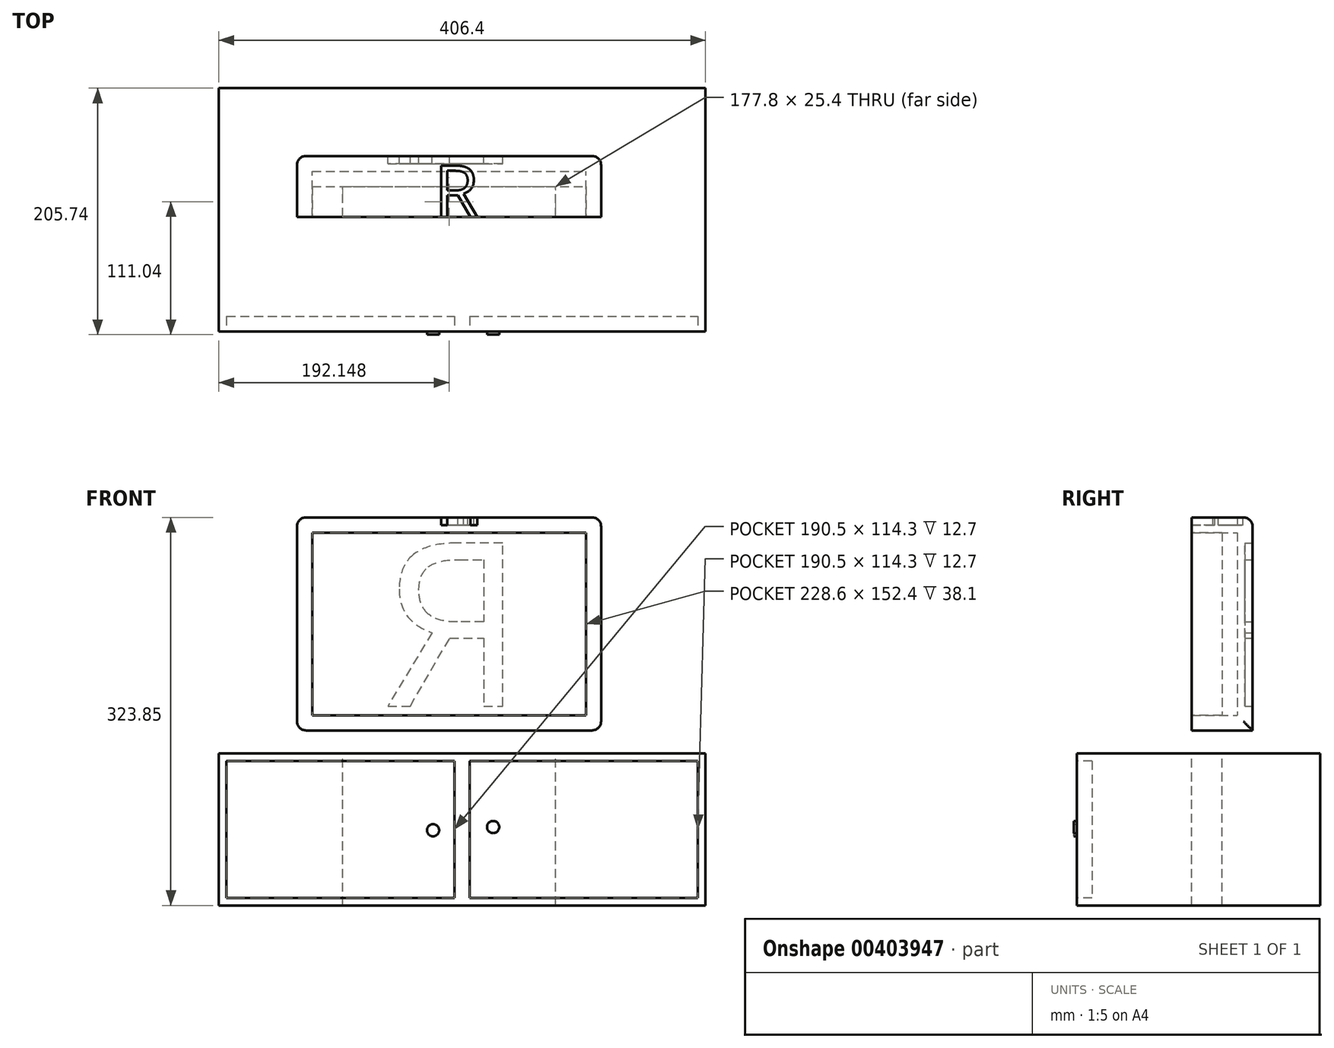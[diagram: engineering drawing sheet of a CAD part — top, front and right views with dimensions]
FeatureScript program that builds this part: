
annotation { "Feature Type Name" : "Feature", "Feature Type Description" : "" }
export const myFeature = defineFeature(function(context is Context, id is Id, definition is map)
    precondition{}
    {
        {
            var Q0;
            Q0=qCreatedBy(makeId("Front.planeOp"),FACE);
            var sketch = newSketch(context, id + "F0", { "sketchPlane" : qUnion([Q0])});
            skLineSegment(sketch, "E0.bottom", {"start": v(-146.56, 129.12) * mm, "end": v(107.44, 129.12) * mm});
            skLineSegment(sketch, "E0.top", {"start": v(-146.56, -48.68) * mm, "end": v(107.44, -48.68) * mm});
            skLineSegment(sketch, "E0.left", {"start": v(-146.56, 129.12) * mm, "end": v(-146.56, -48.68) * mm});
            skLineSegment(sketch, "E0.right", {"start": v(107.44, 129.12) * mm, "end": v(107.44, -48.68) * mm});
            skSolve(sketch);
        }
        {
            var Q0;
            Q0=makeQuery(id+"F0.imprint","IMPRINT",FACE,{"disambiguationData":[TD([[makeQuery(id+"F0.imprint","IMPRINT",EDGE,{"derivedFrom":sQuery(id+"F0.wireOp",EDGE,"E0.bottom")}),-1.0]])]});
            extrude(context, id + "F1", {"entities" : qUnion([Q0]), "depth" : 50.8 * mm});
        }
        {
            var Q0;
            Q0=makeQuery(id+"F1.opExtrude","CAP_FACE",FACE,{"disambiguationData":[OSD([sQuery(id+"F0.wireOp",EDGE,"E0.bottom"),sQuery(id+"F0.wireOp",EDGE,"E0.top"),sQuery(id+"F0.wireOp",EDGE,"E0.left"),sQuery(id+"F0.wireOp",EDGE,"E0.right")])],"isStart":false});
            shell(context, id + "F2", {"entities" : qUnion([Q0]), "thickness" : 12.7 * mm});
        }
        {
            var Q0;
            Q0=makeQuery(id+"F1.opExtrude","CAP_FACE",FACE,{"disambiguationData":[OSD([sQuery(id+"F0.wireOp",EDGE,"E0.bottom"),sQuery(id+"F0.wireOp",EDGE,"E0.top"),sQuery(id+"F0.wireOp",EDGE,"E0.left"),sQuery(id+"F0.wireOp",EDGE,"E0.right")])],"isStart":false});
            var sketch = newSketch(context, id + "F3", { "sketchPlane" : qUnion([Q0])});
            skLineSegment(sketch, "E1.bottom", {"start": v(-108.46, -48.68) * mm, "end": v(69.34, -48.68) * mm});
            skLineSegment(sketch, "E1.top", {"start": v(-108.46, -67.73) * mm, "end": v(69.34, -67.73) * mm});
            skLineSegment(sketch, "E1.left", {"start": v(-108.46, -48.68) * mm, "end": v(-108.46, -67.73) * mm});
            skLineSegment(sketch, "E1.right", {"start": v(69.34, -48.68) * mm, "end": v(69.34, -67.73) * mm});
            skSolve(sketch);
        }
        {
            var Q0;
            Q0 = qConstructionFilter(qBodyType(qCreatedBy(id + "F3" ,EDGE), BodyType.WIRE), ConstructionObject.NO);
            extrude(context, id + "F4", {"bodyType" : ToolBodyType.SURFACE, "surfaceEntities" : qUnion([Q0]), "oppositeDirection" : true, "depth" : 25.4 * mm});
        }
        {
            var Q0;
            Q0=makeQuery(id+"F4.opExtrude","SWEPT_FACE",FACE,{"disambiguationData":[OSD([sQuery(id+"F3.wireOp",EDGE,"E1.top")])]});
            var sketch = newSketch(context, id + "F5", { "sketchPlane" : qUnion([Q0])});
            skLineSegment(sketch, "E2.bottom", {"start": v(-211.7, -146.6) * mm, "end": v(194.7, -146.6) * mm});
            skLineSegment(sketch, "E2.top", {"start": v(-211.7, 56.6) * mm, "end": v(194.7, 56.6) * mm});
            skLineSegment(sketch, "E2.left", {"start": v(-211.7, -146.6) * mm, "end": v(-211.7, 56.6) * mm});
            skLineSegment(sketch, "E2.right", {"start": v(194.7, -146.6) * mm, "end": v(194.7, 56.6) * mm});
            skSolve(sketch);
        }
        {
            var Q0;
            Q0=makeQuery(id+"F5.imprint","IMPRINT",FACE,{"disambiguationData":[TD([[makeQuery(id+"F5.imprint","IMPRINT",EDGE,{"derivedFrom":sQuery(id+"F5.wireOp",EDGE,"E2.bottom")}),1.0]])]});
            extrude(context, id + "F6", {"entities" : qUnion([Q0]), "oppositeDirection" : true, "depth" : 127 * mm});
        }
        {
            var Q0;
            Q0=makeQuery(id+"F6.opExtrude","SWEPT_FACE",FACE,{"disambiguationData":[OSD([sQuery(id+"F5.wireOp",EDGE,"E2.bottom")])]});
            var sketch = newSketch(context, id + "F7", { "sketchPlane" : qUnion([Q0])});
            skLineSegment(sketch, "E3", {"start": v(-8.5, -67.73) * mm, "end": v(-8.5, -194.73) * mm});
            skPoint(sketch, "E3.endSnap0", {"position": v(-8.5, -194.73) * mm});
            skSolve(sketch);
        }
        {
            var Q0;
            {var subQ0=sQuery(id+"F7.wireOp",EDGE,"E3");Q0=makeQuery(id+"F7.imprint","IMPRINT",FACE,{"disambiguationData":[TD([[makeQuery(id+"F7.imprint","IMPRINT",EDGE,{"derivedFrom":subQ0}),-1.0]])]});}
            var sketch = newSketch(context, id + "F8", { "sketchPlane" : qUnion([Q0])});
            skLineSegment(sketch, "E4.bottom", {"start": v(-205.36, -74.08) * mm, "end": v(-14.86, -74.08) * mm});
            skLineSegment(sketch, "E4.top", {"start": v(-205.36, -188.38) * mm, "end": v(-14.86, -188.38) * mm});
            skLineSegment(sketch, "E4.left", {"start": v(-205.36, -74.08) * mm, "end": v(-205.36, -188.38) * mm});
            skLineSegment(sketch, "E4.right", {"start": v(-14.86, -74.08) * mm, "end": v(-14.86, -188.38) * mm});
            skLineSegment(sketch, "E5.bottom", {"start": v(-2.16, -74.08) * mm, "end": v(188.34, -74.08) * mm});
            skLineSegment(sketch, "E5.top", {"start": v(-2.16, -188.38) * mm, "end": v(188.34, -188.38) * mm});
            skLineSegment(sketch, "E5.left", {"start": v(-2.16, -74.08) * mm, "end": v(-2.16, -188.38) * mm});
            skLineSegment(sketch, "E5.right", {"start": v(188.34, -74.08) * mm, "end": v(188.34, -188.38) * mm});
            skSolve(sketch);
        }
        {
            var Q0;
            Q0 = qSketchRegion(id + "F8", true);
            extrude(context, id + "F9", {"entities" : qUnion([Q0]), "operationType" : NewBodyOperationType.REMOVE, "oppositeDirection" : true, "depth" : 12.7 * mm});
        }
        {
            var Q0;
            {var subQ0=sQuery(id+"F7.wireOp",EDGE,"E3");Q0=makeQuery(id+"F7.imprint","IMPRINT",FACE,{"disambiguationData":[TD([[makeQuery(id+"F7.imprint","IMPRINT",EDGE,{"derivedFrom":subQ0}),-1.0]])]});}
            var sketch = newSketch(context, id + "F10", { "sketchPlane" : qUnion([Q0])});
            skCircle(sketch, "E6", {"center": v(-32.88, -132.04) * mm, "radius": 5.08 * mm});
            skCircle(sketch, "E7", {"center": v(17.3, -129.32) * mm, "radius": 5.08 * mm});
            skSolve(sketch);
        }
        {
            var Q0;
            Q0=makeQuery(id+"F1.opExtrude","CAP_FACE",FACE,{"disambiguationData":[OSD([sQuery(id+"F0.wireOp",EDGE,"E0.bottom"),sQuery(id+"F0.wireOp",EDGE,"E0.top"),sQuery(id+"F0.wireOp",EDGE,"E0.left"),sQuery(id+"F0.wireOp",EDGE,"E0.right")])],"isStart":true});
            var sketch = newSketch(context, id + "F11", { "sketchPlane" : qUnion([Q0])});
            skText(sketch, "E8", { "text": "R", "fontName": "OpenSans-Regular.ttf"});
            const initialGuessF11  = {"E8": [-0.04394, -0.02836, 1, 0, 0.13731]};
            skSetInitialGuess(sketch, initialGuessF11);
            skSolve(sketch);
        }
        {
            var Q0;
            Q0 = qSketchRegion(id + "F11", true);
            extrude(context, id + "F12", {"entities" : qUnion([Q0]), "operationType" : NewBodyOperationType.REMOVE, "oppositeDirection" : true, "depth" : 6.35 * mm});
        }
        {
            var Q0;
            Q0=makeQuery(id+"F10.imprint","IMPRINT",FACE,{"disambiguationData":[TD([[makeQuery(id+"F10.imprint","IMPRINT",EDGE,{"derivedFrom":sQuery(id+"F10.wireOp",EDGE,"E6")}),1.0]])]});
            var Q1;
            Q1=makeQuery(id+"F10.imprint","IMPRINT",FACE,{"disambiguationData":[TD([[makeQuery(id+"F10.imprint","IMPRINT",EDGE,{"derivedFrom":sQuery(id+"F10.wireOp",EDGE,"E7")}),1.0]])]});
            extrude(context, id + "F13", {"entities" : qUnion([Q0, Q1]), "depth" : 2.54 * mm});
        }
        {
            var Q0;
            Q0=makeQuery(id+"F1.opExtrude","SWEPT_EDGE",EDGE,{"disambiguationData":[OSD([sQuery(id+"F0.wireOp",EDGE,"E0.bottom"),sQuery(id+"F0.wireOp",EDGE,"E0.right")])]});
            var Q1;
            Q1=makeQuery(id+"F1.opExtrude","CAP_EDGE",EDGE,{"disambiguationData":[OSD([sQuery(id+"F0.wireOp",EDGE,"E0.right")])],"isStart":true});
            var Q2;
            Q2=makeQuery(id+"F1.opExtrude","CAP_EDGE",EDGE,{"disambiguationData":[OSD([sQuery(id+"F0.wireOp",EDGE,"E0.bottom")])],"isStart":true});
            var Q3;
            Q3=makeQuery(id+"F1.opExtrude","SWEPT_EDGE",EDGE,{"disambiguationData":[OSD([sQuery(id+"F0.wireOp",EDGE,"E0.bottom"),sQuery(id+"F0.wireOp",EDGE,"E0.left")])]});
            var Q4;
            Q4=makeQuery(id+"F1.opExtrude","CAP_EDGE",EDGE,{"disambiguationData":[OSD([sQuery(id+"F0.wireOp",EDGE,"E0.left")])],"isStart":true});
            var Q5;
            Q5=makeQuery(id+"F1.opExtrude","SWEPT_EDGE",EDGE,{"disambiguationData":[OSD([sQuery(id+"F0.wireOp",EDGE,"E0.top"),sQuery(id+"F0.wireOp",EDGE,"E0.right")])]});
            var Q6;
            Q6=makeQuery(id+"F1.opExtrude","SWEPT_EDGE",EDGE,{"disambiguationData":[OSD([sQuery(id+"F0.wireOp",EDGE,"E0.top"),sQuery(id+"F0.wireOp",EDGE,"E0.left")])]});
            fillet(context, id + "F14", {"entities" : qUnion([Q0, Q1, Q2, Q3, Q4, Q5, Q6]), "radius" : 7.62 * mm, "tangentPropagation" : true, "allowEdgeOverflow" : false});
        }
        {
            var Q0;
            Q0=makeQuery(id+"F1.opExtrude","CAP_FACE",FACE,{"disambiguationData":[OSD([sQuery(id+"F0.wireOp",EDGE,"E0.bottom"),sQuery(id+"F0.wireOp",EDGE,"E0.top"),sQuery(id+"F0.wireOp",EDGE,"E0.left"),sQuery(id+"F0.wireOp",EDGE,"E0.right")])],"isStart":false});
            var sketch = newSketch(context, id + "F15", { "sketchPlane" : qUnion([Q0])});
            skLineSegment(sketch, "E9.bottom", {"start": v(-133.86, 116.42) * mm, "end": v(94.74, 116.42) * mm});
            skLineSegment(sketch, "E9.top", {"start": v(-133.86, -35.98) * mm, "end": v(94.74, -35.98) * mm});
            skLineSegment(sketch, "E9.left", {"start": v(-133.86, 116.42) * mm, "end": v(-133.86, -35.98) * mm});
            skLineSegment(sketch, "E9.right", {"start": v(94.74, 116.42) * mm, "end": v(94.74, -35.98) * mm});
            skSolve(sketch);
        }
        {
            var Q0;
            Q0=makeQuery(id+"F15.imprint","IMPRINT",FACE,{"disambiguationData":[TD([[makeQuery(id+"F15.imprint","IMPRINT",EDGE,{"derivedFrom":sQuery(id+"F15.wireOp",EDGE,"E9.bottom")}),-1.0]])]});
            extrude(context, id + "F16", {"entities" : qUnion([Q0]), "oppositeDirection" : true, "depth" : 25.4 * mm});
        }
        {
            var Q0;
            Q0=makeQuery(id+"F1.opExtrude","SWEPT_FACE",FACE,{"disambiguationData":[OSD([sQuery(id+"F0.wireOp",EDGE,"E0.bottom")])]});
            var sketch = newSketch(context, id + "F17", { "sketchPlane" : qUnion([Q0])});
            skText(sketch, "E10", { "text": "R", "fontName": "OpenSans-Regular.ttf"});
            const initialGuessF17  = {"E10": [-0.03188, -0.0508, 1, 0, 0.04318]};
            skSetInitialGuess(sketch, initialGuessF17);
            skSolve(sketch);
        }
        {
            var Q0;
            Q0 = qSketchRegion(id + "F17", true);
            extrude(context, id + "F18", {"entities" : qUnion([Q0]), "operationType" : NewBodyOperationType.REMOVE, "oppositeDirection" : true, "depth" : 6.35 * mm});
        }
    });
